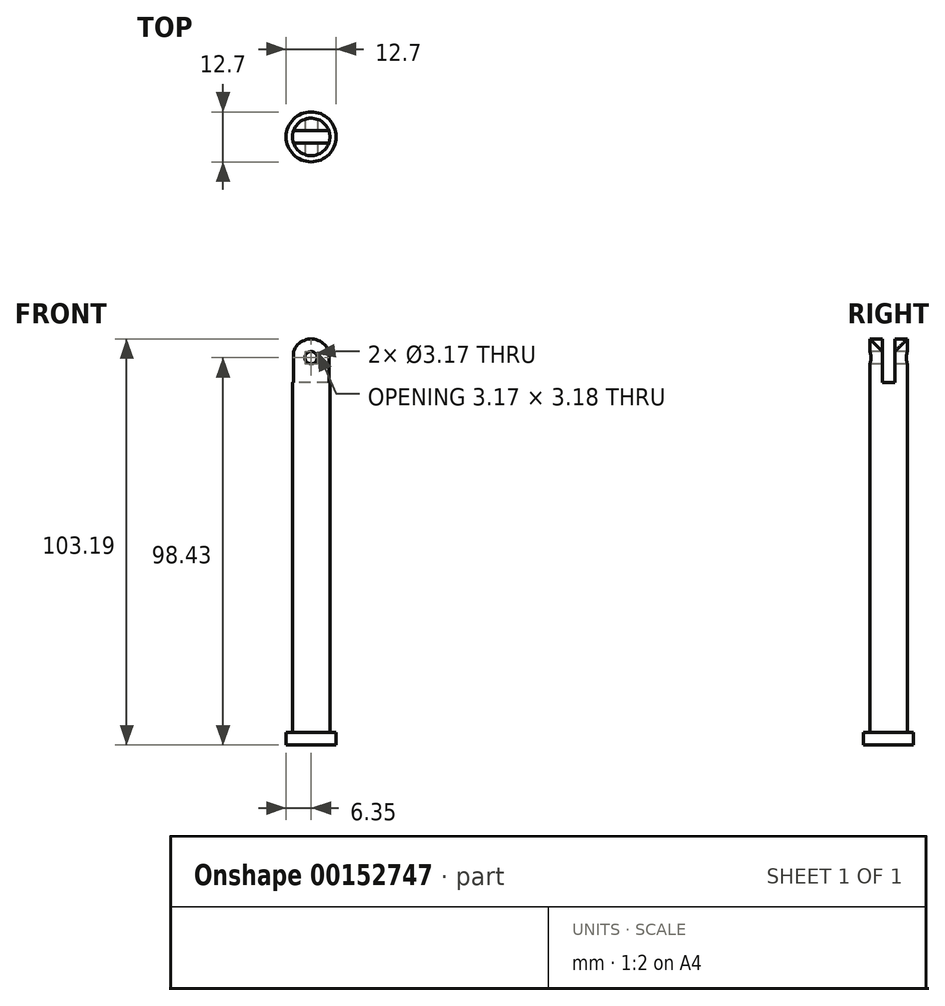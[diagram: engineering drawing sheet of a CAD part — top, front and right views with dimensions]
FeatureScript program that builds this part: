
annotation { "Feature Type Name" : "Feature", "Feature Type Description" : "" }
export const myFeature = defineFeature(function(context is Context, id is Id, definition is map)
    precondition{}
    {
        {
            var Q0;
            Q0=qCreatedBy(makeId("Top.planeOp"),FACE);
            var sketch = newSketch(context, id + "F0", { "sketchPlane" : qUnion([Q0])});
            skCircle(sketch, "E0", {"center": v(0, 0) * mm, "radius": 4.76 * mm});
            skSolve(sketch);
        }
        {
            var Q0;
            Q0 = qSketchRegion(id + "F0", true);
            extrude(context, id + "F1", {"entities" : qUnion([Q0]), "depth" : 101.6 * mm});
        }
        {
            var Q0;
            Q0=makeQuery(id+"F1.opExtrude","CAP_FACE",FACE,{"disambiguationData":[OSD([sQuery(id+"F0.wireOp",EDGE,"E0")])],"isStart":false});
            var sketch = newSketch(context, id + "F2", { "sketchPlane" : qUnion([Q0])});
            skLineSegment(sketch, "E1.bottom", {"start": v(4.76, 1.59) * mm, "end": v(-4.76, 1.59) * mm});
            skLineSegment(sketch, "E1.top", {"start": v(4.76, -1.59) * mm, "end": v(-4.76, -1.59) * mm});
            skLineSegment(sketch, "E1.left", {"start": v(4.76, 1.59) * mm, "end": v(4.76, -1.59) * mm});
            skLineSegment(sketch, "E1.right", {"start": v(-4.76, 1.59) * mm, "end": v(-4.76, -1.59) * mm});
            skPoint(sketch, "E1.middle", {"position": v(0, 0) * mm});
            skSolve(sketch);
        }
        {
            var Q0;
            Q0 = qSketchRegion(id + "F2", true);
            extrude(context, id + "F3", {"entities" : qUnion([Q0]), "operationType" : NewBodyOperationType.REMOVE, "oppositeDirection" : true, "depth" : 12.7 * mm});
        }
        {
            var Q0;
            Q0=qCreatedBy(makeId("Front.planeOp"),FACE);
            var sketch = newSketch(context, id + "F4", { "sketchPlane" : qUnion([Q0])});
            skLineSegment(sketch, "E2.bottom", {"start": v(-4.76, 95.25) * mm, "end": v(4.76, 95.25) * mm, "construction": true});
            skLineSegment(sketch, "E2.top", {"start": v(-4.76, 101.6) * mm, "end": v(4.76, 101.6) * mm});
            skLineSegment(sketch, "E2.left", {"start": v(-4.76, 95.25) * mm, "end": v(-4.76, 101.6) * mm});
            skLineSegment(sketch, "E2.right", {"start": v(4.76, 95.25) * mm, "end": v(4.76, 101.6) * mm});
            skArc(sketch, "E3", {"start": v(4.76, 95.25) * mm, "mid": v(0, 100.01) * mm, "end": v(-4.76, 95.25) * mm});
            skCircle(sketch, "E4", {"center": v(0, 95.25) * mm, "radius": 1.59 * mm});
            skLineSegment(sketch, "E5", {"start": v(0, 95.25) * mm, "end": v(0, 88.9) * mm, "construction": true});
            skSolve(sketch);
        }
        {
            var Q0;
            Q0 = qSketchRegion(id + "F4", true);
            var Q1;
            Q1=makeQuery(id+"F1.opExtrude","SWEPT_FACE",FACE,{"disambiguationData":[OSD([sQuery(id+"F0.wireOp",EDGE,"E0")])]});
            var Q2;
            Q2=makeQuery(id+"F1.opExtrude","SWEPT_FACE",FACE,{"disambiguationData":[OSD([sQuery(id+"F0.wireOp",EDGE,"E0")])]});
            extrude(context, id + "F5", {"entities" : qUnion([Q0]), "operationType" : NewBodyOperationType.REMOVE, "endBound" : BoundingType.UP_TO_SURFACE, "oppositeDirection" : true, "endBoundEntityFace" : qUnion([Q1]), "depth" : 25.4 * mm, "hasSecondDirection" : true, "secondDirectionBound" : SecondDirectionBoundingType.UP_TO_SURFACE, "secondDirectionOppositeDirection" : false, "secondDirectionBoundEntityFace" : qUnion([Q2]), "secondDirectionDepth" : 25.4 * mm});
        }
        {
            var Q0;
            Q0=makeQuery(id+"F1.opExtrude","CAP_FACE",FACE,{"disambiguationData":[OSD([sQuery(id+"F0.wireOp",EDGE,"E0")])],"isStart":true});
            var sketch = newSketch(context, id + "F6", { "sketchPlane" : qUnion([Q0])});
            skCircle(sketch, "E6", {"center": v(0, 0) * mm, "radius": 6.35 * mm});
            skSolve(sketch);
        }
        {
            var Q0;
            Q0 = qSketchRegion(id + "F6", true);
            extrude(context, id + "F7", {"entities" : qUnion([Q0]), "operationType" : NewBodyOperationType.ADD, "depth" : 3.17 * mm});
        }
    });
